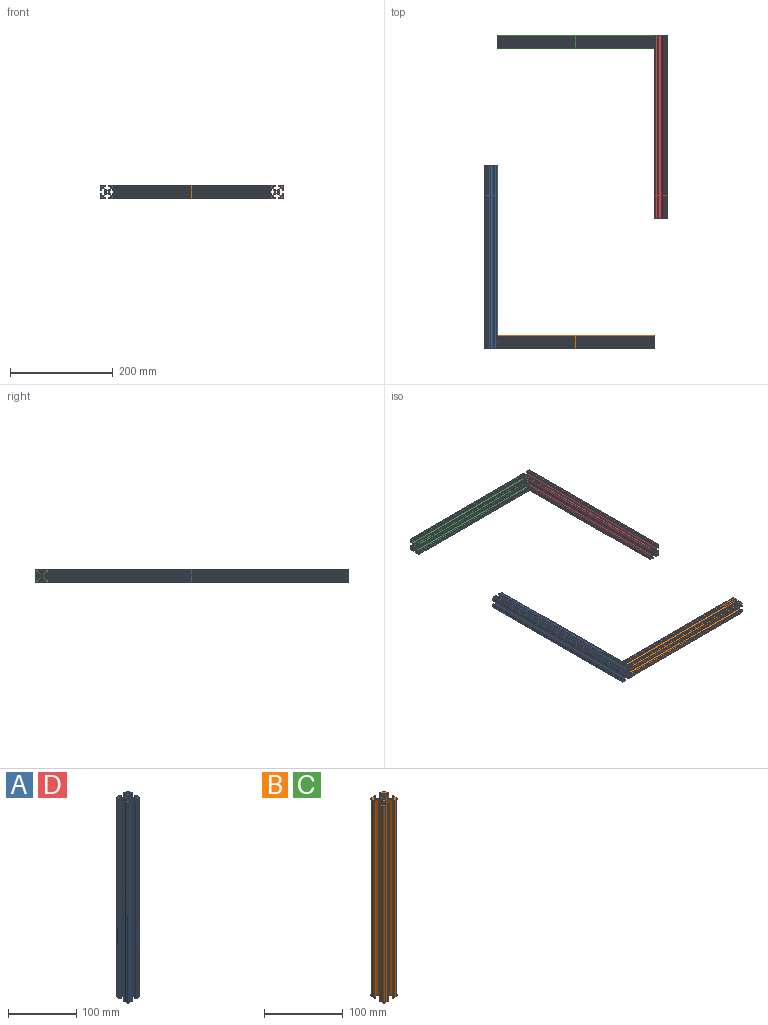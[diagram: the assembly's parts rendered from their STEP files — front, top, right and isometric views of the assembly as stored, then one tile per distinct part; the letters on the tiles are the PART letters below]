
ASSEMBLY  parts=4 mates=9
PART A: 83 faces, bbox 25.4x25.4x355.6 mm
  f0: plane 355.6x2.13mm, normal (1,0,0), area 757.9mm2, adj f1,f41,f81,f82
  f1: cylinder r=1.02mm len=355.6mm, axis (0,0,1), area 851.3mm2, adj f0,f2,f81,f82
  f2: plane 355.6x3.33mm, normal (-0.71,0.71,0), area 1674.7mm2, adj f1,f3,f81,f82
  f3: cylinder r=3.17mm len=355.6mm, axis (0,0,1), area 886.7mm2, adj f2,f4,f81,f82
  f4: plane 355.6x3.24mm, normal (-1,0,0), area 1150.8mm2, adj f3,f5,f81,f82
  f5: cylinder r=3.17mm len=355.6mm, axis (0,0,1), area 886.7mm2, adj f4,f6,f81,f82
  f6: plane 355.6x3.33mm, normal (-0.71,-0.71,0), area 1674.7mm2, adj f5,f7,f81,f82
  f7: cylinder r=1.02mm len=355.6mm, axis (0,0,1), area 851.3mm2, adj f6,f8,f81,f82
  f8: plane 355.6x2.13mm, normal (1,0,0), area 757.9mm2, adj f7,f42,f81,f82
  f9: plane 355.6x2.13mm, normal (0,-1,0), area 757.9mm2, adj f10,f52,f81,f82
  f10: cylinder r=1.02mm len=355.6mm, axis (0,0,1), area 851.3mm2, adj f9,f11,f81,f82
  f11: plane 355.6x3.33mm, normal (0.71,0.71,0), area 1674.7mm2, adj f10,f12,f81,f82
  f12: cylinder r=3.17mm len=355.6mm, axis (0,0,1), area 886.7mm2, adj f11,f13,f81,f82
  f13: plane 355.6x3.24mm, normal (0,1,0), area 1150.8mm2, adj f12,f14,f81,f82
  f14: cylinder r=3.17mm len=355.6mm, axis (0,0,1), area 886.7mm2, adj f13,f15,f81,f82
  f15: plane 355.6x3.33mm, normal (-0.71,0.71,0), area 1674.7mm2, adj f14,f16,f81,f82
  f16: cylinder r=1.02mm len=355.6mm, axis (0,0,1), area 851.3mm2, adj f15,f17,f81,f82
  f17: plane 355.6x2.13mm, normal (0,-1,0), area 757.9mm2, adj f16,f53,f81,f82
  f18: plane 355.6x2.13mm, normal (-1,0,0), area 757.9mm2, adj f19,f63,f81,f82
  f19: cylinder r=1.02mm len=355.6mm, axis (0,0,1), area 851.3mm2, adj f18,f20,f81,f82
  f20: plane 355.6x3.33mm, normal (0.71,-0.71,0), area 1674.7mm2, adj f19,f21,f81,f82
  f21: cylinder r=3.17mm len=355.6mm, axis (0,0,1), area 886.7mm2, adj f20,f22,f81,f82
  f22: plane 355.6x3.24mm, normal (1,0,0), area 1150.8mm2, adj f21,f23,f81,f82
  f23: cylinder r=3.17mm len=355.6mm, axis (0,0,1), area 886.7mm2, adj f22,f24,f81,f82
  f24: plane 355.6x3.33mm, normal (0.71,0.71,0), area 1674.7mm2, adj f23,f25,f81,f82
  f25: cylinder r=1.02mm len=355.6mm, axis (0,0,1), area 851.3mm2, adj f24,f26,f81,f82
  f26: plane 355.6x2.13mm, normal (-1,0,0), area 757.9mm2, adj f25,f64,f81,f82
  f27: plane 355.6x2.13mm, normal (0,1,0), area 757.9mm2, adj f28,f74,f81,f82
  f28: cylinder r=1.02mm len=355.6mm, axis (0,0,1), area 851.3mm2, adj f27,f29,f81,f82
  f29: plane 355.6x3.33mm, normal (-0.71,-0.71,0), area 1674.7mm2, adj f28,f30,f81,f82
  f30: cylinder r=3.17mm len=355.6mm, axis (0,0,1), area 886.7mm2, adj f29,f31,f81,f82
  f31: plane 355.6x3.24mm, normal (0,-1,0), area 1150.8mm2, adj f30,f32,f81,f82
  f32: cylinder r=3.17mm len=355.6mm, axis (0,0,1), area 886.7mm2, adj f31,f33,f81,f82
  f33: plane 355.6x3.33mm, normal (0.71,-0.71,0), area 1674.7mm2, adj f32,f34,f81,f82
  f34: cylinder r=1.02mm len=355.6mm, axis (0,0,1), area 851.3mm2, adj f33,f35,f81,f82
  f35: plane 355.6x2.13mm, normal (0,1,0), area 757.9mm2, adj f34,f75,f81,f82
  f36: cylinder r=2.6mm len=355.6mm, axis (0,0,1), area 5817mm2, adj f81,f82
  f37: cylinder r=0.51mm len=355.6mm, axis (0,0,1), area 567.5mm2, adj f38,f80,f81,f82
  f38: plane 355.6x3.22mm, normal (-1,0,0), area 1144.1mm2, adj f37,f39,f81,f82
  f39: cylinder r=0.51mm len=355.6mm, axis (0,0,1), area 567.5mm2, adj f38,f40,f81,f82
  f40: plane 355.6x0.97mm, normal (-1,0,0), area 346.2mm2, adj f39,f41,f81,f82
  f41: cylinder r=1.1mm len=355.6mm, axis (0,0,1), area 1234.3mm2, adj f0,f40,f81,f82
  f42: cylinder r=1.1mm len=355.6mm, axis (0,0,1), area 1234.3mm2, adj f8,f43,f81,f82
  f43: plane 355.6x0.97mm, normal (-1,0,0), area 346.2mm2, adj f42,f44,f81,f82
  f44: cylinder r=0.51mm len=355.6mm, axis (0,0,1), area 567.5mm2, adj f43,f45,f81,f82
  f45: plane 355.6x3.22mm, normal (-1,0,0), area 1144.1mm2, adj f44,f46,f81,f82
  f46: cylinder r=0.51mm len=355.6mm, axis (0,0,1), area 567.5mm2, adj f45,f47,f81,f82
  f47: cylinder r=2.11mm len=355.6mm, axis (0,0,1), area 1195.7mm2, adj f46,f48,f81,f82
  f48: cylinder r=0.51mm len=355.6mm, axis (0,0,1), area 567.5mm2, adj f47,f49,f81,f82
  f49: plane 355.6x3.22mm, normal (0,1,0), area 1144.1mm2, adj f48,f50,f81,f82
  f50: cylinder r=0.51mm len=355.6mm, axis (0,0,1), area 567.5mm2, adj f49,f51,f81,f82
  f51: plane 355.6x0.97mm, normal (0,1,0), area 346.2mm2, adj f50,f52,f81,f82
  f52: cylinder r=1.1mm len=355.6mm, axis (0,0,1), area 1234.3mm2, adj f9,f51,f81,f82
  f53: cylinder r=1.1mm len=355.6mm, axis (0,0,1), area 1234.3mm2, adj f17,f54,f81,f82
  f54: plane 355.6x0.97mm, normal (0,1,0), area 346.2mm2, adj f53,f55,f81,f82
  f55: cylinder r=0.51mm len=355.6mm, axis (0,0,1), area 567.5mm2, adj f54,f56,f81,f82
  f56: plane 355.6x3.22mm, normal (0,1,0), area 1144.1mm2, adj f55,f57,f81,f82
  f57: cylinder r=0.51mm len=355.6mm, axis (0,0,1), area 567.5mm2, adj f56,f58,f81,f82
  f58: cylinder r=2.11mm len=355.6mm, axis (0,0,1), area 1195.7mm2, adj f57,f59,f81,f82
  f59: cylinder r=0.51mm len=355.6mm, axis (0,0,1), area 567.5mm2, adj f58,f60,f81,f82
  f60: plane 355.6x3.22mm, normal (1,0,0), area 1144.1mm2, adj f59,f61,f81,f82
  f61: cylinder r=0.51mm len=355.6mm, axis (0,0,1), area 567.5mm2, adj f60,f62,f81,f82
  f62: plane 355.6x0.97mm, normal (1,0,0), area 346.2mm2, adj f61,f63,f81,f82
  f63: cylinder r=1.1mm len=355.6mm, axis (0,0,1), area 1234.3mm2, adj f18,f62,f81,f82
  f64: cylinder r=1.1mm len=355.6mm, axis (0,0,1), area 1234.3mm2, adj f26,f65,f81,f82
  f65: plane 355.6x0.97mm, normal (1,0,0), area 346.2mm2, adj f64,f66,f81,f82
  f66: cylinder r=0.51mm len=355.6mm, axis (0,0,1), area 567.5mm2, adj f65,f67,f81,f82
  f67: plane 355.6x3.22mm, normal (1,0,0), area 1144.1mm2, adj f66,f68,f81,f82
  f68: cylinder r=0.51mm len=355.6mm, axis (0,0,1), area 567.5mm2, adj f67,f69,f81,f82
  f69: cylinder r=2.11mm len=355.6mm, axis (0,0,1), area 1195.7mm2, adj f68,f70,f81,f82
  f70: cylinder r=0.51mm len=355.6mm, axis (0,0,1), area 567.5mm2, adj f69,f71,f81,f82
  f71: plane 355.6x3.22mm, normal (0,-1,0), area 1144.1mm2, adj f70,f72,f81,f82
  f72: cylinder r=0.51mm len=355.6mm, axis (0,0,1), area 567.5mm2, adj f71,f73,f81,f82
  f73: plane 355.6x0.97mm, normal (0,-1,0), area 346.2mm2, adj f72,f74,f81,f82
  f74: cylinder r=1.1mm len=355.6mm, axis (0,0,1), area 1234.3mm2, adj f27,f73,f81,f82
  f75: cylinder r=1.1mm len=355.6mm, axis (0,0,1), area 1234.3mm2, adj f35,f76,f81,f82
  f76: plane 355.6x0.97mm, normal (0,-1,0), area 346.2mm2, adj f75,f77,f81,f82
  f77: cylinder r=0.51mm len=355.6mm, axis (0,0,1), area 567.5mm2, adj f76,f78,f81,f82
  f78: plane 355.6x3.22mm, normal (0,-1,0), area 1144.1mm2, adj f77,f79,f81,f82
  f79: cylinder r=0.51mm len=355.6mm, axis (0,0,1), area 567.5mm2, adj f78,f80,f81,f82
  f80: cylinder r=2.11mm len=355.6mm, axis (0,0,1), area 1195.7mm2, adj f37,f79,f81,f82
  f81: plane 25.4x25.4mm, normal (0,0,-1), area 279.7mm2, adj f0,f1,f2,f3,f4,f5,f6,f7
  f82: plane 25.4x25.4mm, normal (0,0,1), area 279.7mm2, adj f0,f1,f2,f3,f4,f5,f6,f7
PART B: 83 faces, bbox 25.4x25.4x304.8 mm
  f0: cylinder r=0.51mm len=304.8mm, axis (0,0,1), area 486.4mm2, adj f1,f79,f81,f82
  f1: plane 304.8x3.22mm, normal (-1,0,0), area 980.6mm2, adj f0,f2,f81,f82
  f2: cylinder r=0.51mm len=304.8mm, axis (0,0,1), area 486.4mm2, adj f1,f3,f81,f82
  f3: plane 304.8x0.97mm, normal (-1,0,0), area 296.8mm2, adj f2,f4,f81,f82
  f4: cylinder r=1.1mm len=304.8mm, axis (0,0,1), area 1058mm2, adj f3,f5,f81,f82
  f5: plane 304.8x2.13mm, normal (1,0,0), area 649.6mm2, adj f4,f6,f81,f82
  f6: cylinder r=1.02mm len=304.8mm, axis (0,0,1), area 729.7mm2, adj f5,f7,f81,f82
  f7: plane 304.8x3.33mm, normal (-0.71,0.71,0), area 1435.4mm2, adj f6,f8,f81,f82
  f8: cylinder r=3.17mm len=304.8mm, axis (0,0,1), area 760.1mm2, adj f7,f9,f81,f82
  f9: plane 304.8x3.24mm, normal (-1,0,0), area 986.4mm2, adj f8,f10,f81,f82
  f10: cylinder r=3.17mm len=304.8mm, axis (0,0,1), area 760.1mm2, adj f9,f11,f81,f82
  f11: plane 304.8x3.33mm, normal (-0.71,-0.71,0), area 1435.4mm2, adj f10,f12,f81,f82
  f12: cylinder r=1.02mm len=304.8mm, axis (0,0,1), area 729.7mm2, adj f11,f13,f81,f82
  f13: plane 304.8x2.13mm, normal (1,0,0), area 649.6mm2, adj f12,f14,f81,f82
  f14: cylinder r=1.1mm len=304.8mm, axis (0,0,1), area 1058mm2, adj f13,f15,f81,f82
  f15: plane 304.8x0.97mm, normal (-1,0,0), area 296.8mm2, adj f14,f16,f81,f82
  f16: cylinder r=0.51mm len=304.8mm, axis (0,0,1), area 486.4mm2, adj f15,f17,f81,f82
  f17: plane 304.8x3.22mm, normal (-1,0,0), area 980.6mm2, adj f16,f18,f81,f82
  f18: cylinder r=0.51mm len=304.8mm, axis (0,0,1), area 486.4mm2, adj f17,f19,f81,f82
  f19: cylinder r=2.11mm len=304.8mm, axis (0,0,1), area 1024.8mm2, adj f18,f20,f81,f82
  f20: cylinder r=0.51mm len=304.8mm, axis (0,0,1), area 486.4mm2, adj f19,f21,f81,f82
  f21: plane 304.8x3.22mm, normal (0,1,0), area 980.6mm2, adj f20,f22,f81,f82
  f22: cylinder r=0.51mm len=304.8mm, axis (0,0,1), area 486.4mm2, adj f21,f23,f81,f82
  f23: plane 304.8x0.97mm, normal (0,1,0), area 296.8mm2, adj f22,f24,f81,f82
  f24: cylinder r=1.1mm len=304.8mm, axis (0,0,1), area 1058mm2, adj f23,f25,f81,f82
  f25: plane 304.8x2.13mm, normal (0,-1,0), area 649.6mm2, adj f24,f26,f81,f82
  f26: cylinder r=1.02mm len=304.8mm, axis (0,0,1), area 729.7mm2, adj f25,f27,f81,f82
  f27: plane 304.8x3.33mm, normal (0.71,0.71,0), area 1435.4mm2, adj f26,f28,f81,f82
  f28: cylinder r=3.17mm len=304.8mm, axis (0,0,1), area 760.1mm2, adj f27,f29,f81,f82
  f29: plane 304.8x3.24mm, normal (0,1,0), area 986.4mm2, adj f28,f30,f81,f82
  f30: cylinder r=3.17mm len=304.8mm, axis (0,0,1), area 760.1mm2, adj f29,f31,f81,f82
  f31: plane 304.8x3.33mm, normal (-0.71,0.71,0), area 1435.4mm2, adj f30,f32,f81,f82
  f32: cylinder r=1.02mm len=304.8mm, axis (0,0,1), area 729.7mm2, adj f31,f33,f81,f82
  f33: plane 304.8x2.13mm, normal (0,-1,0), area 649.6mm2, adj f32,f34,f81,f82
  f34: cylinder r=1.1mm len=304.8mm, axis (0,0,1), area 1058mm2, adj f33,f35,f81,f82
  f35: plane 304.8x0.97mm, normal (0,1,0), area 296.8mm2, adj f34,f36,f81,f82
  f36: cylinder r=0.51mm len=304.8mm, axis (0,0,1), area 486.4mm2, adj f35,f37,f81,f82
  f37: plane 304.8x3.22mm, normal (0,1,0), area 980.6mm2, adj f36,f38,f81,f82
  f38: cylinder r=0.51mm len=304.8mm, axis (0,0,1), area 486.4mm2, adj f37,f39,f81,f82
  f39: cylinder r=2.11mm len=304.8mm, axis (0,0,1), area 1024.8mm2, adj f38,f40,f81,f82
  f40: cylinder r=0.51mm len=304.8mm, axis (0,0,1), area 486.4mm2, adj f39,f41,f81,f82
  f41: plane 304.8x3.22mm, normal (1,0,0), area 980.6mm2, adj f40,f42,f81,f82
  f42: cylinder r=0.51mm len=304.8mm, axis (0,0,1), area 486.4mm2, adj f41,f43,f81,f82
  f43: plane 304.8x0.97mm, normal (1,0,0), area 296.8mm2, adj f42,f44,f81,f82
  f44: cylinder r=1.1mm len=304.8mm, axis (0,0,1), area 1058mm2, adj f43,f45,f81,f82
  f45: plane 304.8x2.13mm, normal (-1,0,0), area 649.6mm2, adj f44,f46,f81,f82
  f46: cylinder r=1.02mm len=304.8mm, axis (0,0,1), area 729.7mm2, adj f45,f47,f81,f82
  f47: plane 304.8x3.33mm, normal (0.71,-0.71,0), area 1435.4mm2, adj f46,f48,f81,f82
  f48: cylinder r=3.17mm len=304.8mm, axis (0,0,1), area 760.1mm2, adj f47,f49,f81,f82
  f49: plane 304.8x3.24mm, normal (1,0,0), area 986.4mm2, adj f48,f50,f81,f82
  f50: cylinder r=3.17mm len=304.8mm, axis (0,0,1), area 760.1mm2, adj f49,f51,f81,f82
  f51: plane 304.8x3.33mm, normal (0.71,0.71,0), area 1435.4mm2, adj f50,f52,f81,f82
  f52: cylinder r=1.02mm len=304.8mm, axis (0,0,1), area 729.7mm2, adj f51,f53,f81,f82
  f53: plane 304.8x2.13mm, normal (-1,0,0), area 649.6mm2, adj f52,f54,f81,f82
  f54: cylinder r=1.1mm len=304.8mm, axis (0,0,1), area 1058mm2, adj f53,f55,f81,f82
  f55: plane 304.8x0.97mm, normal (1,0,0), area 296.8mm2, adj f54,f56,f81,f82
  f56: cylinder r=0.51mm len=304.8mm, axis (0,0,1), area 486.4mm2, adj f55,f57,f81,f82
  f57: plane 304.8x3.22mm, normal (1,0,0), area 980.6mm2, adj f56,f58,f81,f82
  f58: cylinder r=0.51mm len=304.8mm, axis (0,0,1), area 486.4mm2, adj f57,f59,f81,f82
  f59: cylinder r=2.11mm len=304.8mm, axis (0,0,1), area 1024.8mm2, adj f58,f60,f81,f82
  f60: cylinder r=0.51mm len=304.8mm, axis (0,0,1), area 486.4mm2, adj f59,f61,f81,f82
  f61: plane 304.8x3.22mm, normal (0,-1,0), area 980.6mm2, adj f60,f62,f81,f82
  f62: cylinder r=0.51mm len=304.8mm, axis (0,0,1), area 486.4mm2, adj f61,f63,f81,f82
  f63: plane 304.8x0.97mm, normal (0,-1,0), area 296.8mm2, adj f62,f64,f81,f82
  f64: cylinder r=1.1mm len=304.8mm, axis (0,0,1), area 1058mm2, adj f63,f65,f81,f82
  f65: plane 304.8x2.13mm, normal (0,1,0), area 649.6mm2, adj f64,f66,f81,f82
  f66: cylinder r=1.02mm len=304.8mm, axis (0,0,1), area 729.7mm2, adj f65,f67,f81,f82
  f67: plane 304.8x3.33mm, normal (-0.71,-0.71,0), area 1435.4mm2, adj f66,f68,f81,f82
  f68: cylinder r=3.17mm len=304.8mm, axis (0,0,1), area 760.1mm2, adj f67,f69,f81,f82
  f69: plane 304.8x3.24mm, normal (0,-1,0), area 986.4mm2, adj f68,f70,f81,f82
  f70: cylinder r=3.17mm len=304.8mm, axis (0,0,1), area 760.1mm2, adj f69,f71,f81,f82
  f71: plane 304.8x3.33mm, normal (0.71,-0.71,0), area 1435.4mm2, adj f70,f72,f81,f82
  f72: cylinder r=1.02mm len=304.8mm, axis (0,0,1), area 729.7mm2, adj f71,f73,f81,f82
  f73: plane 304.8x2.13mm, normal (0,1,0), area 649.6mm2, adj f72,f74,f81,f82
  f74: cylinder r=1.1mm len=304.8mm, axis (0,0,1), area 1058mm2, adj f73,f75,f81,f82
  f75: plane 304.8x0.97mm, normal (0,-1,0), area 296.8mm2, adj f74,f76,f81,f82
  f76: cylinder r=0.51mm len=304.8mm, axis (0,0,1), area 486.4mm2, adj f75,f77,f81,f82
  f77: plane 304.8x3.22mm, normal (0,-1,0), area 980.6mm2, adj f76,f78,f81,f82
  f78: cylinder r=0.51mm len=304.8mm, axis (0,0,1), area 486.4mm2, adj f77,f79,f81,f82
  f79: cylinder r=2.11mm len=304.8mm, axis (0,0,1), area 1024.8mm2, adj f0,f78,f81,f82
  f80: cylinder r=2.6mm len=304.8mm, axis (0,0,1), area 4986mm2, adj f81,f82
  f81: plane 25.4x25.4mm, normal (0,0,-1), area 279.7mm2, adj f0,f1,f2,f3,f4,f5,f6,f7
  f82: plane 25.4x25.4mm, normal (0,0,1), area 279.7mm2, adj f0,f1,f2,f3,f4,f5,f6,f7
PART C: same geometry as B
PART D: same geometry as A
PLACE A rot(axis=(-1,0,0),90deg) t=(7.94,304.8,-12.7)mm fixed
PLACE B rot(axis=(0.58,-0.58,-0.58),120deg) t=(20.64,-292.1,-12.7)mm
PLACE C rot(axis=(0.58,-0.58,-0.58),120deg) t=(20.64,292.1,-12.7)mm
PLACE D rot(axis=(0.58,0.58,-0.58),120deg) t=(338.14,-304.8,-12.7)mm
MATE planar C.f21 <-> A.f71  axis (0,0,1) through (173.04,300.04,0)mm
MATE planar D.f45 <-> B.f37  axis (0,0,1) through (346.08,127,0)mm
MATE planar C.f59 <-> A.f67  axis (-1,0,0) through (20.64,281.51,-23.29)mm
MATE parallel C.f37 <-> A.f71  axis (0,0,1) through (173.04,284.16,0)mm
MATE planar B.f41 <-> A.f36  axis (0,-1,0) through (173.04,-304.8,-4.76)mm
MATE parallel B.f37 <-> A.f71  axis (0,0,1) through (173.04,-300.04,0)mm
MATE planar B.f82 <-> A.f67  axis (-1,0,0) through (20.64,-300.86,-19.89)mm
MATE planar B.f39 <-> D.f78  axis (1,0,0) through (325.44,-302.69,-2.11)mm
MATE planar B.f37 <-> A.f71  axis (0,0,1) through (173.04,-300.04,0)mm
